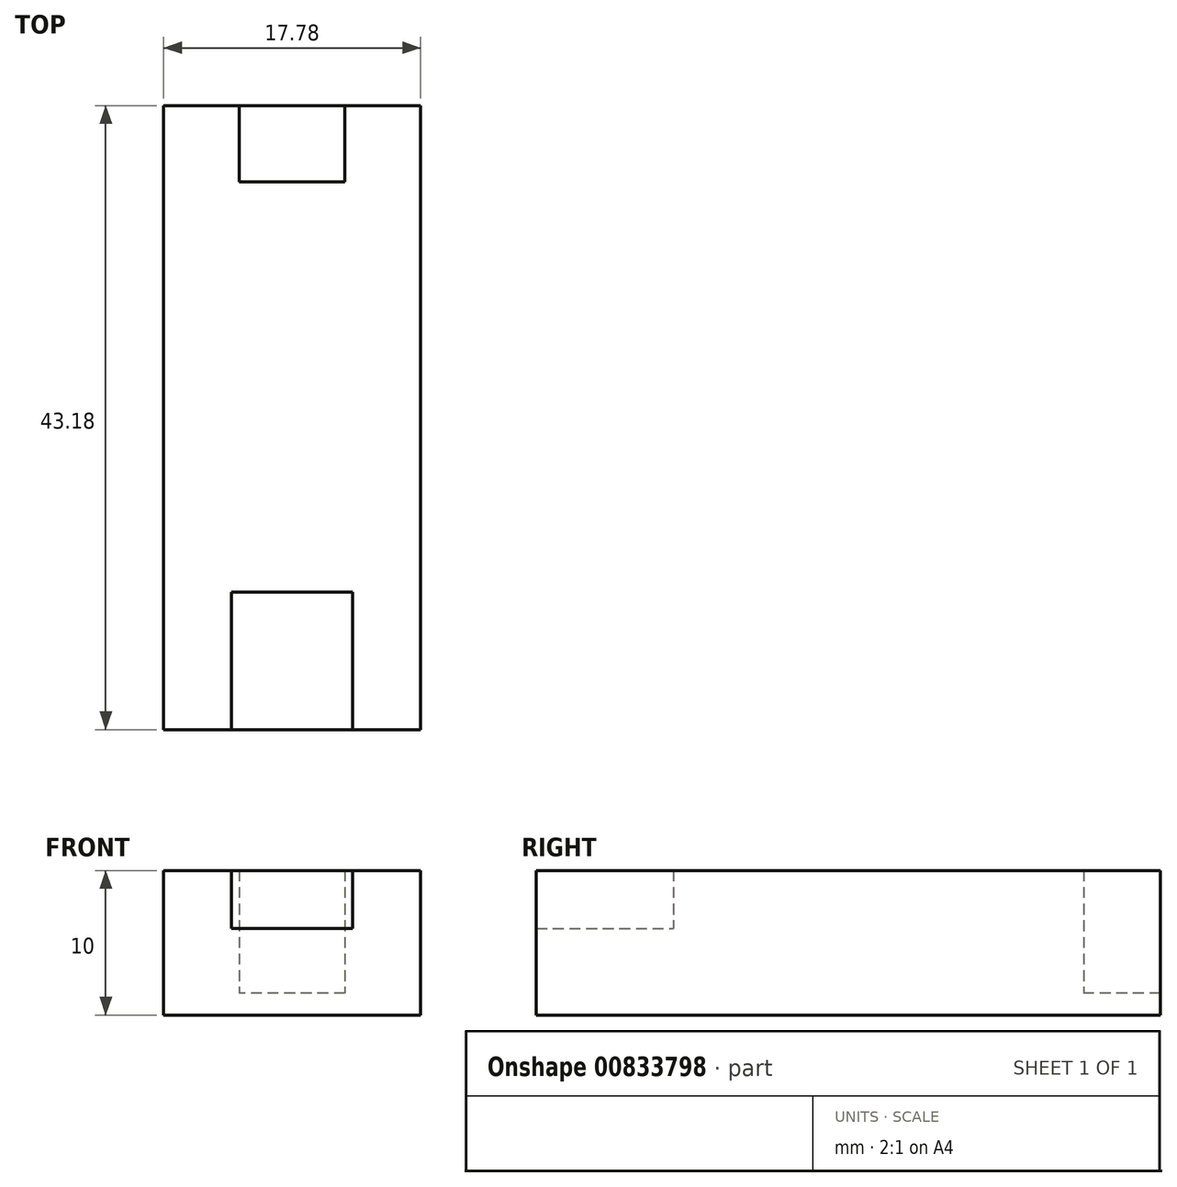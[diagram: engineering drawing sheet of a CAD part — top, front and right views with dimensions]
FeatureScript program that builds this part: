
annotation { "Feature Type Name" : "Feature", "Feature Type Description" : "" }
export const myFeature = defineFeature(function(context is Context, id is Id, definition is map)
    precondition{}
    {
        {
            var Q0;
            Q0=qCreatedBy(makeId("Top.planeOp"),FACE);
            var sketch = newSketch(context, id + "F0", { "sketchPlane" : qUnion([Q0])});
            skLineSegment(sketch, "E0.bottom", {"start": v(8.9, -21.6) * mm, "end": v(-8.89, -21.6) * mm});
            skLineSegment(sketch, "E0.top", {"start": v(8.9, 21.59) * mm, "end": v(-8.89, 21.59) * mm});
            skLineSegment(sketch, "E0.left", {"start": v(8.9, -21.59) * mm, "end": v(8.9, 21.59) * mm});
            skLineSegment(sketch, "E0.right", {"start": v(-8.89, -21.6) * mm, "end": v(-8.89, 21.59) * mm});
            skPoint(sketch, "E0.middle", {"position": v(0, 0) * mm});
            skSolve(sketch);
        }
        {
            var Q0;
            Q0 = qSketchRegion(id + "F0", true);
            extrude(context, id + "F1", {"entities" : qUnion([Q0]), "depth" : 1.5 * mm, "offsetDistance" : 25 * mm});
        }
        {
            var Q0;
            Q0=makeQuery(id+"F1.opExtrude","CAP_FACE",FACE,{"disambiguationData":[OSD([sQuery(id+"F0.wireOp",EDGE,"E0.bottom"),sQuery(id+"F0.wireOp",EDGE,"E0.top"),sQuery(id+"F0.wireOp",EDGE,"E0.left"),sQuery(id+"F0.wireOp",EDGE,"E0.right")])],"isStart":false});
            var sketch = newSketch(context, id + "F2", { "sketchPlane" : qUnion([Q0])});
            skLineSegment(sketch, "E1.bottom", {"start": v(-3.65, 21.59) * mm, "end": v(3.65, 21.59) * mm});
            skLineSegment(sketch, "E1.top", {"start": v(-3.65, 16.29) * mm, "end": v(3.65, 16.29) * mm});
            skLineSegment(sketch, "E1.left", {"start": v(-3.65, 21.59) * mm, "end": v(-3.65, 16.29) * mm});
            skLineSegment(sketch, "E1.right", {"start": v(3.65, 21.59) * mm, "end": v(3.65, 16.29) * mm});
            skPoint(sketch, "E1.middle", {"position": v(0, 18.94) * mm});
            skPoint(sketch, "E1.middle.positionSnap0", {"position": v(0, 21.59) * mm});
            skPoint(sketch, "E1.centerSnap0", {"position": v(0, 21.59) * mm});
            skLineSegment(sketch, "E2.bottom", {"start": v(-4.19, -21.6) * mm, "end": v(4.19, -21.6) * mm});
            skLineSegment(sketch, "E2.top", {"start": v(-4.19, -12.1) * mm, "end": v(4.19, -12.1) * mm});
            skLineSegment(sketch, "E2.left", {"start": v(-4.19, -21.6) * mm, "end": v(-4.19, -12.1) * mm});
            skLineSegment(sketch, "E2.right", {"start": v(4.19, -21.6) * mm, "end": v(4.19, -12.1) * mm});
            skPoint(sketch, "E2.middle", {"position": v(0, -16.84) * mm});
            skPoint(sketch, "E2.middle.positionSnap0", {"position": v(0, -21.6) * mm});
            skPoint(sketch, "E2.centerSnap0", {"position": v(0, -21.6) * mm});
            skSolve(sketch);
        }
        {
            var Q0;
            Q0=makeQuery(id+"F2.imprint","IMPRINT",FACE,{"disambiguationData":[TD([[makeQuery(id+"F2.imprint","IMPRINT",EDGE,{"derivedFrom":sQuery(id+"F2.wireOp",EDGE,"E1.top")}),-1.0]])]});
            extrude(context, id + "F3", {"entities" : qUnion([Q0]), "operationType" : NewBodyOperationType.ADD, "depth" : 8.5 * mm, "offsetDistance" : 25 * mm});
        }
        {
            var Q0;
            {var subQ2=sQuery(id+"F0.wireOp",EDGE,"E0.bottom");var subQ3=sQuery(id+"F0.wireOp",EDGE,"E0.left");var subQ6=sQuery(id+"F0.wireOp",EDGE,"E0.right");Q0=makeQuery(id+"F3.boolean.opBoolean","SPLIT",FACE,{"disambiguationData":[TD([makeQuery(id+"F1.opExtrude","SWEPT_FACE",FACE,{"disambiguationData":[OSD([subQ2])]})])],"derivedFrom":makeQuery(id+"F1.opExtrude","CAP_FACE",FACE,{"disambiguationData":[OSD([subQ2,sQuery(id+"F0.wireOp",EDGE,"E0.top"),subQ3,subQ6])],"isStart":false})});}
            extrude(context, id + "F4", {"entities" : qUnion([Q0]), "operationType" : NewBodyOperationType.ADD, "depth" : 4.5 * mm, "offsetDistance" : 25 * mm});
        }
    });
